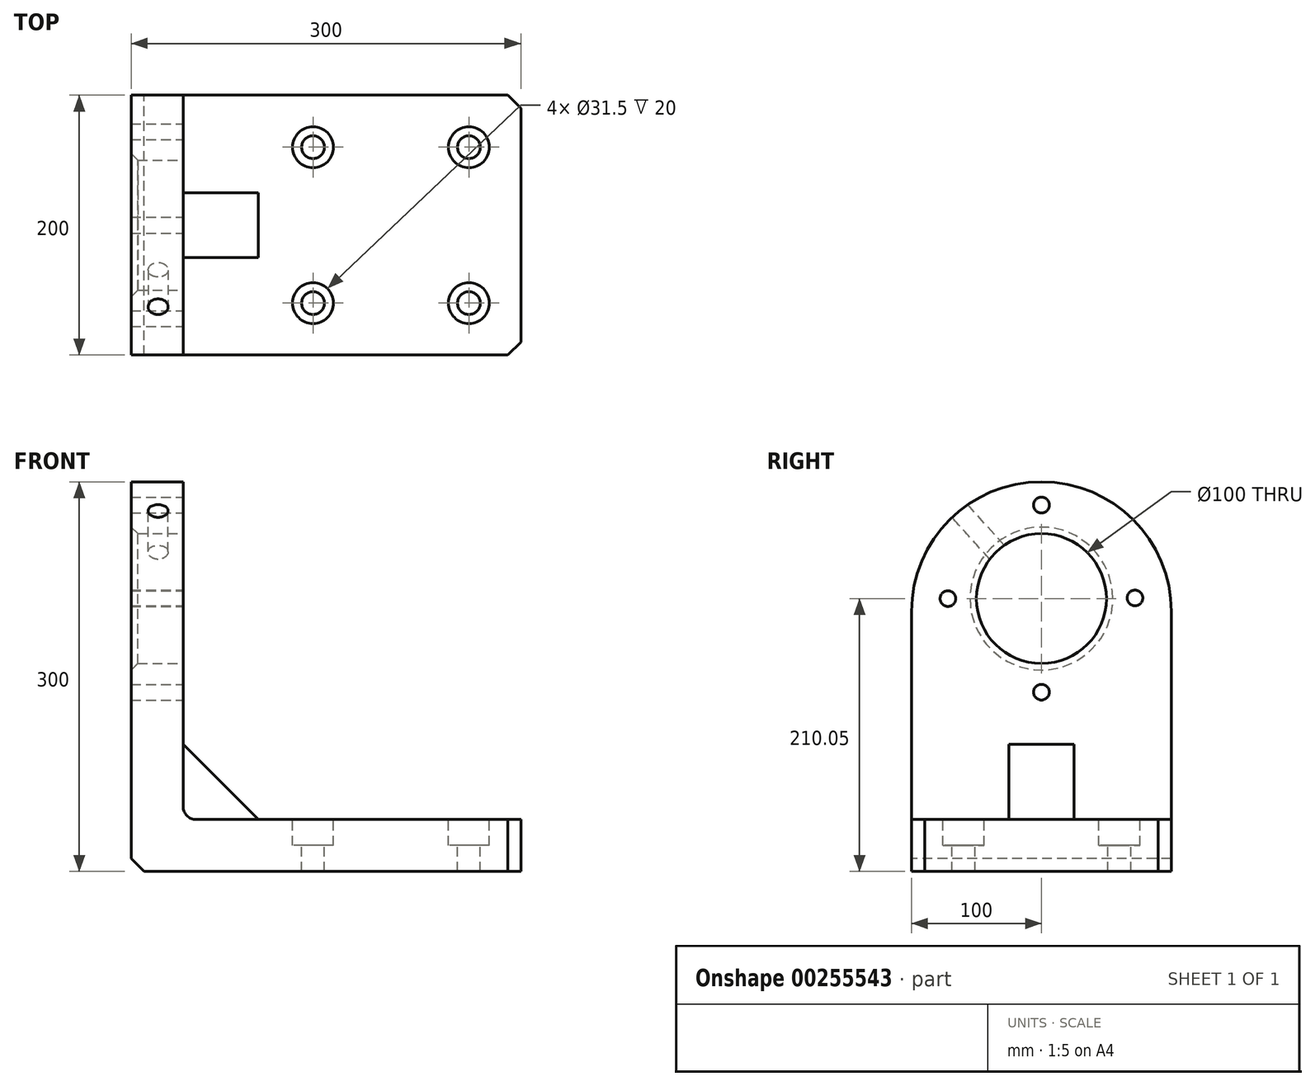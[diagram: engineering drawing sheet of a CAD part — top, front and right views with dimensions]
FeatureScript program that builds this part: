
annotation { "Feature Type Name" : "Feature", "Feature Type Description" : "" }
export const myFeature = defineFeature(function(context is Context, id is Id, definition is map)
    precondition{}
    {
        {
            var Q0;
            Q0=qCreatedBy(makeId("Top.planeOp"),FACE);
            var sketch = newSketch(context, id + "F0", { "sketchPlane" : qUnion([Q0])});
            skLineSegment(sketch, "E0.bottom", {"start": v(150, 100) * mm, "end": v(-150, 100) * mm});
            skLineSegment(sketch, "E0.top", {"start": v(150, -100) * mm, "end": v(-150, -100) * mm});
            skLineSegment(sketch, "E0.left", {"start": v(150, 100) * mm, "end": v(150, -100) * mm});
            skLineSegment(sketch, "E0.right", {"start": v(-150, 100) * mm, "end": v(-150, -100) * mm});
            skPoint(sketch, "E0.middle", {"position": v(0, 0) * mm});
            skSolve(sketch);
        }
        {
            var Q0;
            Q0 = qSketchRegion(id + "F0", true);
            extrude(context, id + "F1", {"entities" : qUnion([Q0]), "depth" : 300 * mm});
        }
        {
            var Q0;
            Q0=makeQuery(id+"F1.opExtrude","SWEPT_FACE",FACE,{"disambiguationData":[OSD([sQuery(id+"F0.wireOp",EDGE,"E0.top")])]});
            var sketch = newSketch(context, id + "F2", { "sketchPlane" : qUnion([Q0])});
            skLineSegment(sketch, "E1.bottom", {"start": v(150, 300) * mm, "end": v(-110, 300) * mm});
            skLineSegment(sketch, "E1.top", {"start": v(150, 40) * mm, "end": v(-110, 40) * mm});
            skLineSegment(sketch, "E1.left", {"start": v(150, 300) * mm, "end": v(150, 40) * mm});
            skLineSegment(sketch, "E1.right", {"start": v(-110, 300) * mm, "end": v(-110, 40) * mm});
            skSolve(sketch);
        }
        {
            var Q0;
            Q0=makeQuery(id+"F2.imprint","IMPRINT",FACE,{"disambiguationData":[TD([[makeQuery(id+"F2.imprint","IMPRINT",EDGE,{"derivedFrom":sQuery(id+"F2.wireOp",EDGE,"E1.bottom")}),1.0]])]});
            extrude(context, id + "F3", {"entities" : qUnion([Q0]), "operationType" : NewBodyOperationType.REMOVE, "oppositeDirection" : true, "depth" : 421.64 * mm});
        }
        {
            var Q0;
            Q0=makeQuery(id+"F1.opExtrude","SWEPT_EDGE",EDGE,{"disambiguationData":[OSD([sQuery(id+"F0.wireOp",EDGE,"E0.top"),sQuery(id+"F0.wireOp",EDGE,"E0.left")])]});
            var Q1;
            Q1=makeQuery(id+"F1.opExtrude","SWEPT_EDGE",EDGE,{"disambiguationData":[OSD([sQuery(id+"F0.wireOp",EDGE,"E0.bottom"),sQuery(id+"F0.wireOp",EDGE,"E0.left")])]});
            chamfer(context, id + "F4", {"entities" : qUnion([Q0, Q1]), "width" : 10 * mm, "tangentPropagation" : true});
        }
        {
            var Q0;
            Q0=makeQuery(id+"F3.boolean.opBoolean","COPY",EDGE,{"derivedFrom":makeQuery(id+"F3.opExtrude","SWEPT_EDGE",EDGE,{"disambiguationData":[OSD([sQuery(id+"F2.wireOp",EDGE,"E1.top"),sQuery(id+"F2.wireOp",EDGE,"E1.right")])]})});
            fillet(context, id + "F5", {"entities" : qUnion([Q0]), "radius" : 10 * mm, "tangentPropagation" : true, "allowEdgeOverflow" : false});
        }
        {
            var Q0;
            Q0=makeQuery(id+"F1.opExtrude","CAP_EDGE",EDGE,{"disambiguationData":[OSD([sQuery(id+"F0.wireOp",EDGE,"E0.right")])],"isStart":true});
            chamfer(context, id + "F6", {"entities" : qUnion([Q0]), "width" : 10 * mm, "tangentPropagation" : true});
        }
        {
            var Q0;
            Q0=makeQuery(id+"F3.boolean.opBoolean","COPY",FACE,{"derivedFrom":makeQuery(id+"F3.opExtrude","SWEPT_FACE",FACE,{"disambiguationData":[OSD([sQuery(id+"F2.wireOp",EDGE,"E1.top")])]})});
            var sketch = newSketch(context, id + "F7", { "sketchPlane" : qUnion([Q0])});
            skCircle(sketch, "E2", {"center": v(110, 60) * mm, "radius": 8.75 * mm});
            skCircle(sketch, "E3", {"center": v(110, -60) * mm, "radius": 8.75 * mm});
            skCircle(sketch, "E4", {"center": v(-10, 60) * mm, "radius": 8.75 * mm});
            skCircle(sketch, "E5", {"center": v(-10, -60) * mm, "radius": 8.75 * mm});
            skCircle(sketch, "E6", {"center": v(110, 60) * mm, "radius": 15.75 * mm});
            skCircle(sketch, "E7", {"center": v(-10, 60) * mm, "radius": 15.75 * mm});
            skCircle(sketch, "E8", {"center": v(-10, -60) * mm, "radius": 15.75 * mm});
            skCircle(sketch, "E9", {"center": v(110, -60) * mm, "radius": 15.75 * mm});
            skSolve(sketch);
        }
        {
            var Q0;
            Q0=makeQuery(id+"F7.imprint","IMPRINT",FACE,{"disambiguationData":[TD([[makeQuery(id+"F7.imprint","IMPRINT",EDGE,{"derivedFrom":sQuery(id+"F7.wireOp",EDGE,"E3")}),1.0]])]});
            var Q1;
            Q1=makeQuery(id+"F7.imprint","IMPRINT",FACE,{"disambiguationData":[TD([[makeQuery(id+"F7.imprint","IMPRINT",EDGE,{"derivedFrom":sQuery(id+"F7.wireOp",EDGE,"E2")}),1.0]])]});
            var Q2;
            Q2=makeQuery(id+"F7.imprint","IMPRINT",FACE,{"disambiguationData":[TD([[makeQuery(id+"F7.imprint","IMPRINT",EDGE,{"derivedFrom":sQuery(id+"F7.wireOp",EDGE,"E4")}),1.0]])]});
            var Q3;
            Q3=makeQuery(id+"F7.imprint","IMPRINT",FACE,{"disambiguationData":[TD([[makeQuery(id+"F7.imprint","IMPRINT",EDGE,{"derivedFrom":sQuery(id+"F7.wireOp",EDGE,"E5")}),1.0]])]});
            extrude(context, id + "F8", {"entities" : qUnion([Q0, Q1, Q2, Q3]), "operationType" : NewBodyOperationType.REMOVE, "oppositeDirection" : true, "depth" : 79.5 * mm});
        }
        {
            var Q0;
            Q0=makeQuery(id+"F7.imprint","IMPRINT",FACE,{"disambiguationData":[TD([[makeQuery(id+"F7.imprint","IMPRINT",EDGE,{"derivedFrom":sQuery(id+"F7.wireOp",EDGE,"E4")}),-1.0]])]});
            var Q1;
            Q1=makeQuery(id+"F7.imprint","IMPRINT",FACE,{"disambiguationData":[TD([[makeQuery(id+"F7.imprint","IMPRINT",EDGE,{"derivedFrom":sQuery(id+"F7.wireOp",EDGE,"E5")}),-1.0]])]});
            var Q2;
            Q2=makeQuery(id+"F7.imprint","IMPRINT",FACE,{"disambiguationData":[TD([[makeQuery(id+"F7.imprint","IMPRINT",EDGE,{"derivedFrom":sQuery(id+"F7.wireOp",EDGE,"E3")}),-1.0]])]});
            var Q3;
            Q3=makeQuery(id+"F7.imprint","IMPRINT",FACE,{"disambiguationData":[TD([[makeQuery(id+"F7.imprint","IMPRINT",EDGE,{"derivedFrom":sQuery(id+"F7.wireOp",EDGE,"E2")}),-1.0]])]});
            extrude(context, id + "F9", {"entities" : qUnion([Q0, Q1, Q2, Q3]), "operationType" : NewBodyOperationType.REMOVE, "oppositeDirection" : true, "depth" : 20 * mm});
        }
        {
            var Q0;
            Q0=makeQuery(id+"F1.opExtrude","CAP_EDGE",EDGE,{"disambiguationData":[OSD([sQuery(id+"F0.wireOp",EDGE,"E0.top")])],"isStart":false});
            var Q1;
            Q1=makeQuery(id+"F1.opExtrude","CAP_EDGE",EDGE,{"disambiguationData":[OSD([sQuery(id+"F0.wireOp",EDGE,"E0.bottom")])],"isStart":false});
            fillet(context, id + "F10", {"entities" : qUnion([Q0, Q1]), "radius" : 100 * mm, "tangentPropagation" : true, "allowEdgeOverflow" : false});
        }
        {
            var Q0;
            Q0=makeQuery(id+"F3.boolean.opBoolean","COPY",FACE,{"derivedFrom":makeQuery(id+"F3.opExtrude","SWEPT_FACE",FACE,{"disambiguationData":[OSD([sQuery(id+"F2.wireOp",EDGE,"E1.right")])]})});
            var sketch = newSketch(context, id + "F11", { "sketchPlane" : qUnion([Q0])});
            skLineSegment(sketch, "E10", {"start": v(0, 300) * mm, "end": v(0, 50) * mm, "construction": true});
            skCircle(sketch, "E11", {"center": v(0, 210.05) * mm, "radius": 50 * mm});
            skCircle(sketch, "E12", {"center": v(0, 210.05) * mm, "radius": 72 * mm, "construction": true});
            skCircle(sketch, "E13", {"center": v(0, 282.05) * mm, "radius": 8.82 * mm});
            skCircle(sketch, "E14", {"center": v(0, 138.05) * mm, "radius": 10.87 * mm});
            skCircle(sketch, "E15", {"center": v(72, 210.54) * mm, "radius": 10.3 * mm});
            skCircle(sketch, "E16", {"center": v(-72, 210.05) * mm, "radius": 9.93 * mm});
            skSolve(sketch);
        }
        {
            var Q0;
            Q0=makeQuery(id+"F11.imprint","IMPRINT",FACE,{"disambiguationData":[TD([[makeQuery(id+"F11.imprint","IMPRINT",EDGE,{"derivedFrom":sQuery(id+"F11.wireOp",EDGE,"E11")}),1.0]])]});
            extrude(context, id + "F12", {"entities" : qUnion([Q0]), "operationType" : NewBodyOperationType.REMOVE, "oppositeDirection" : true, "depth" : 145.03 * mm});
        }
        {
            var Q0;
            Q0=sQuery(id+"F11.wireOp",VERTEX,"E16.center");
            var Q1;
            Q1=sQuery(id+"F11.wireOp",VERTEX,"E13.center");
            var Q2;
            Q2=sQuery(id+"F11.wireOp",VERTEX,"E15.center");
            var Q3;
            Q3=sQuery(id+"F11.wireOp",VERTEX,"E14.center");
            var Q4;
            Q4=makeQuery(id+"F1.opExtrude","SWEPT_BODY",BODY,{"disambiguationData":[OSD([sQuery(id+"F0.wireOp",EDGE,"E0.bottom"),sQuery(id+"F0.wireOp",EDGE,"E0.top"),sQuery(id+"F0.wireOp",EDGE,"E0.left"),sQuery(id+"F0.wireOp",EDGE,"E0.right")])]});
            hole(context, id + "F13", {"style" : HoleStyle.SIMPLE, "endStyle" : HoleEndStyle.THROUGH, "standardTappedOrClearance" : lookupTablePath({ "standard" : "ISO", "engagement" : "75%", "pitch" : "2 mm", "size" : "M14", "type" : "Tapped" }), "standardBlindInLast" : lookupTablePath({ "standard" : "ISO", "engagement" : "75%", "pitch" : "2 mm", "size" : "M14", "type" : "Tapped" }), "holeDiameter" : 12.1 * mm, "showTappedDepth" : true, "tappedDepth" : 12.7 * mm, "tapClearance" : 3, "locations" : qUnion([Q0, Q1, Q2, Q3]), "scope" : qUnion([Q4]), "majorDiameter" : 14 * mm});
        }
        {
            var Q0;
            Q0=makeQuery(id+"F12.boolean.opBoolean","INTERSECT",EDGE,{"derivedFrom":[makeQuery(id+"F1.opExtrude","SWEPT_FACE",FACE,{"disambiguationData":[OSD([sQuery(id+"F0.wireOp",EDGE,"E0.right")])]}),makeQuery(id+"F12.opExtrude","SWEPT_FACE",FACE,{"disambiguationData":[OSD([sQuery(id+"F11.wireOp",EDGE,"E11")])]})]});
            var Q1;
            Q1=makeQuery(id+"F12.boolean.opBoolean","COPY",EDGE,{"derivedFrom":makeQuery(id+"F12.opExtrude","CAP_EDGE",EDGE,{"disambiguationData":[OSD([sQuery(id+"F11.wireOp",EDGE,"E11")])],"isStart":true})});
            chamfer(context, id + "F14", {"entities" : qUnion([Q0, Q1]), "width" : 5 * mm, "tangentPropagation" : true});
        }
        {
            var Q0;
            Q0=qCreatedBy(makeId("Front.planeOp"),FACE);
            var sketch = newSketch(context, id + "F15", { "sketchPlane" : qUnion([Q0])});
            skLineSegment(sketch, "E17.bottom", {"start": v(-111.58, 99.57) * mm, "end": v(-20.9, 99.57) * mm});
            skLineSegment(sketch, "E17.top", {"start": v(-111.58, 39.57) * mm, "end": v(-20.9, 39.57) * mm});
            skLineSegment(sketch, "E17.left", {"start": v(-111.58, 99.57) * mm, "end": v(-111.58, 39.57) * mm});
            skLineSegment(sketch, "E17.right", {"start": v(-20.9, 99.57) * mm, "end": v(-20.9, 39.57) * mm});
            skLineSegment(sketch, "E18", {"start": v(-111.58, 99.57) * mm, "end": v(-51.58, 39.57) * mm});
            skSolve(sketch);
        }
        {
            var Q0;
            {var subQ0=sQuery(id+"F15.wireOp",EDGE,"E17.left");Q0=makeQuery(id+"F15.imprint","IMPRINT",FACE,{"disambiguationData":[TD([[makeQuery(id+"F15.imprint","IMPRINT",EDGE,{"derivedFrom":subQ0}),1.0]])]});}
            extrude(context, id + "F16", {"entities" : qUnion([Q0]), "operationType" : NewBodyOperationType.ADD, "endBound" : BoundingType.SYMMETRIC, "depth" : 50 * mm});
        }
        {
            var Q0;
            Q0=makeQuery(id+"F3.boolean.opBoolean","COPY",FACE,{"derivedFrom":makeQuery(id+"F3.opExtrude","SWEPT_FACE",FACE,{"disambiguationData":[OSD([sQuery(id+"F2.wireOp",EDGE,"E1.right")])]})});
            var sketch = newSketch(context, id + "F17", { "sketchPlane" : qUnion([Q0])});
            skLineSegment(sketch, "E19", {"start": v(0, 200) * mm, "end": v(-66.69, 274.52) * mm});
            skLineSegment(sketch, "E20", {"start": v(0, 200) * mm, "end": v(-120.6, 206.68) * mm, "construction": true});
            skSolve(sketch);
        }
        {
            var Q0;
            Q0=sQuery(id+"F17.wireOp",VERTEX,"E19.end");
            var Q1;
            Q1=sQuery(id+"F17.wireOp",EDGE,"E19");
            cPlane(context, id + "F18", {"entities" : qUnion([Q0, Q1]), "cplaneType" : CPlaneType.LINE_POINT, "offset" : 25.4 * mm, "width" : 152.4 * mm, "height" : 152.4 * mm});
        }
        {
            var Q0;
            Q0=qCreatedBy(id+"F18.planeOp",FACE);
            var sketch = newSketch(context, id + "F19", { "sketchPlane" : qUnion([Q0])});
            skCircle(sketch, "E21", {"center": v(-129.28, 138.3) * mm, "radius": 6.5 * mm});
            skSolve(sketch);
        }
        {
            var Q0;
            Q0=sQuery(id+"F19.wireOp",VERTEX,"E21.center");
            var Q1;
            Q1=makeQuery(id+"F1.opExtrude","SWEPT_BODY",BODY,{"disambiguationData":[OSD([sQuery(id+"F0.wireOp",EDGE,"E0.bottom"),sQuery(id+"F0.wireOp",EDGE,"E0.top"),sQuery(id+"F0.wireOp",EDGE,"E0.left"),sQuery(id+"F0.wireOp",EDGE,"E0.right")])]});
            hole(context, id + "F20", {"style" : HoleStyle.SIMPLE, "endStyle" : HoleEndStyle.BLIND, "standardTappedOrClearance" : lookupTablePath({ "standard" : "ISO", "fit" : "Normal", "size" : "M14", "type" : "Clearance" }), "standardBlindInLast" : lookupTablePath({ "fit" : "Standard", "standard" : "ISO", "size" : "M14", "type" : "Clearance" }), "holeDiameter" : 15.5 * mm, "holeDepth" : 44.1 * mm, "tappedDepth" : 12.7 * mm, "tapClearance" : 3, "locations" : qUnion([Q0]), "scope" : qUnion([Q1])});
        }
    });
